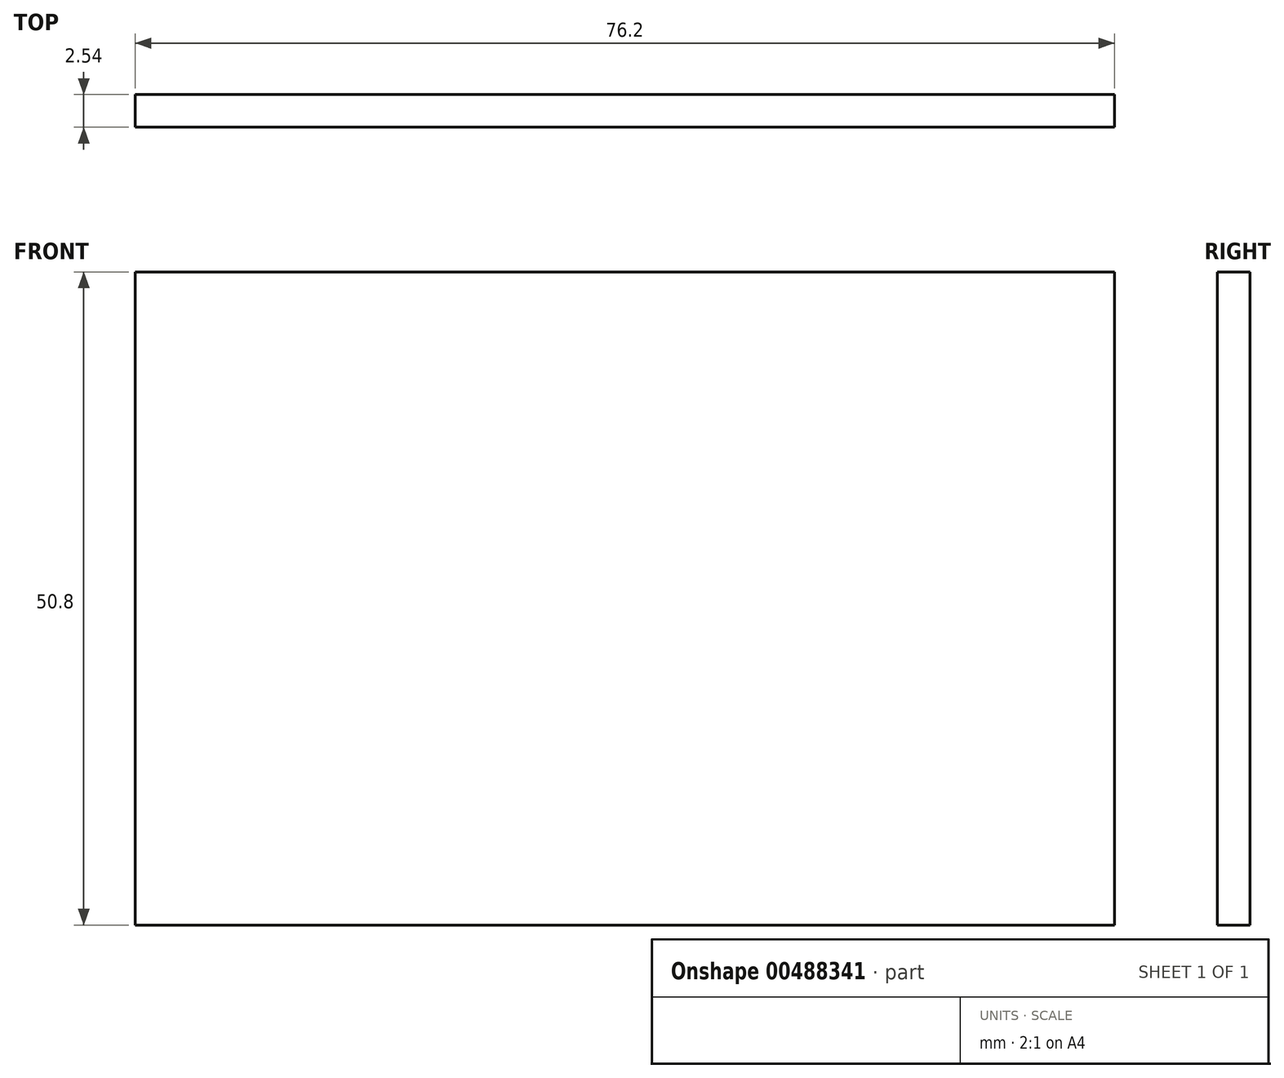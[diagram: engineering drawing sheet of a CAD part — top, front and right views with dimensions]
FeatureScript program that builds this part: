
annotation { "Feature Type Name" : "Feature", "Feature Type Description" : "" }
export const myFeature = defineFeature(function(context is Context, id is Id, definition is map)
    precondition{}
    {
        {
            var Q0;
            Q0=qCreatedBy(makeId("Front.planeOp"),FACE);
            var sketch = newSketch(context, id + "F0", { "sketchPlane" : qUnion([Q0])});
            skLineSegment(sketch, "E0.bottom", {"start": v(-76.2, 50.8) * mm, "end": v(0, 50.8) * mm});
            skLineSegment(sketch, "E0.top", {"start": v(-76.2, 0) * mm, "end": v(0, 0) * mm});
            skLineSegment(sketch, "E0.left", {"start": v(-76.2, 50.8) * mm, "end": v(-76.2, 0) * mm});
            skLineSegment(sketch, "E0.right", {"start": v(0, 50.8) * mm, "end": v(0, 0) * mm});
            skSolve(sketch);
        }
        {
            var Q0;
            Q0=makeQuery(id+"F0.imprint","IMPRINT",FACE,{"disambiguationData":[TD([[makeQuery(id+"F0.imprint","IMPRINT",EDGE,{"derivedFrom":sQuery(id+"F0.wireOp",EDGE,"E0.bottom")}),-1.0]])]});
            extrude(context, id + "F1", {"entities" : qUnion([Q0]), "depth" : 2.54 * mm});
        }
    });
